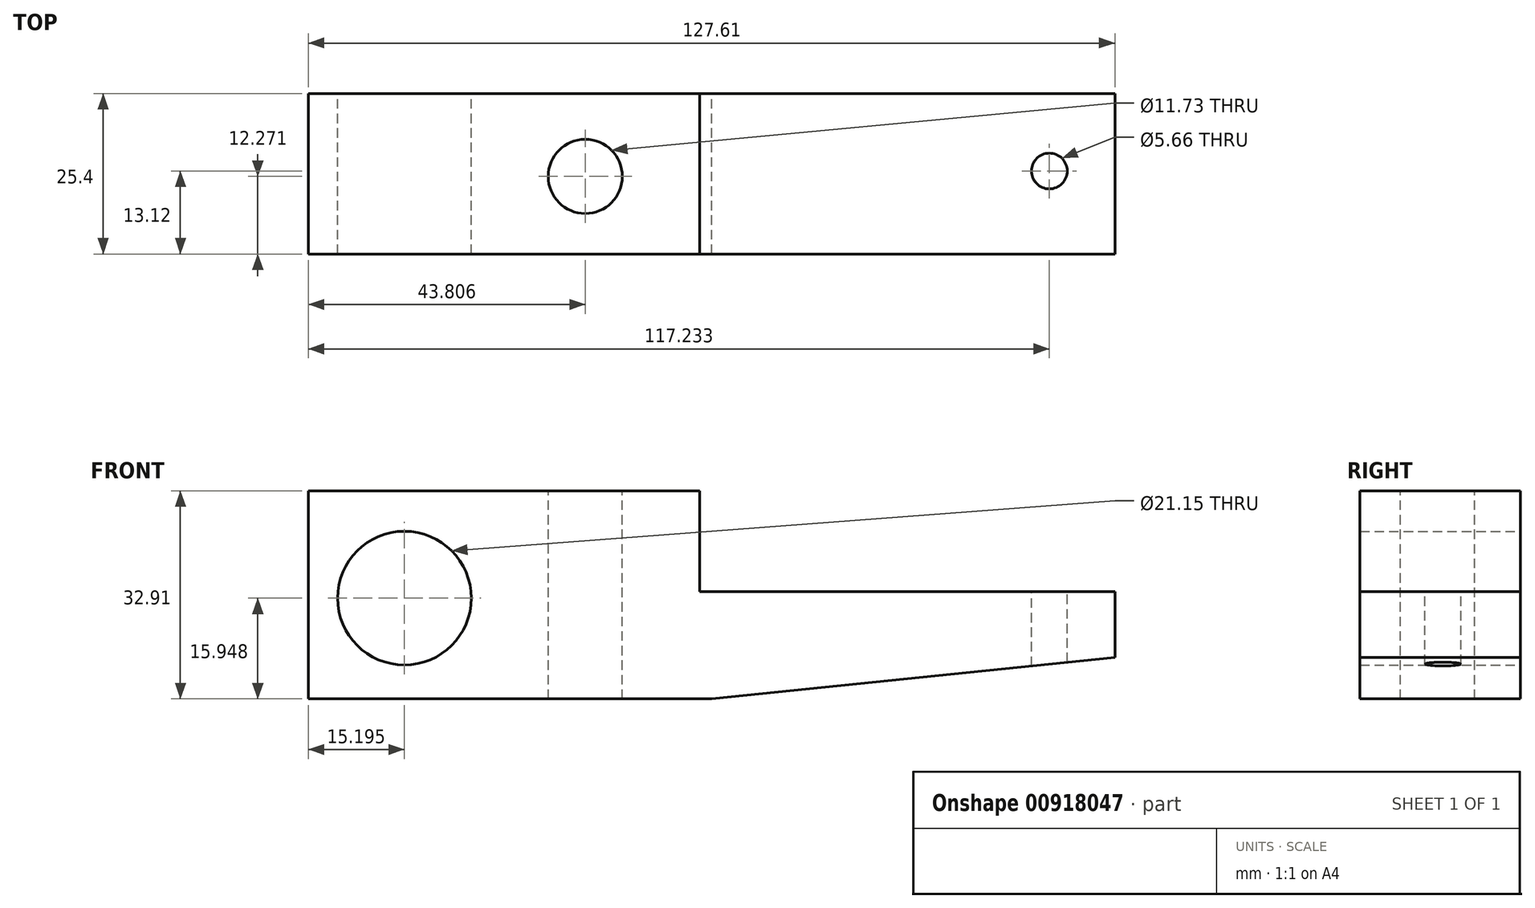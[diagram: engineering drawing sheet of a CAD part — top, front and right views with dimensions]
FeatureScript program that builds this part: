
annotation { "Feature Type Name" : "Feature", "Feature Type Description" : "" }
export const myFeature = defineFeature(function(context is Context, id is Id, definition is map)
    precondition{}
    {
        {
            var Q0;
            Q0=qCreatedBy(makeId("Front.planeOp"),FACE);
            var sketch = newSketch(context, id + "F0", { "sketchPlane" : qUnion([Q0])});
            skLineSegment(sketch, "E0.bottom", {"start": v(-61.9, 38.61) * mm, "end": v(65.7, 38.61) * mm});
            skLineSegment(sketch, "E0.top", {"start": v(-61.9, 5.7) * mm, "end": v(65.7, 5.7) * mm});
            skLineSegment(sketch, "E0.left", {"start": v(-61.9, 38.61) * mm, "end": v(-61.9, 5.7) * mm});
            skLineSegment(sketch, "E0.right", {"start": v(65.7, 38.61) * mm, "end": v(65.7, 5.7) * mm});
            skCircle(sketch, "E1", {"center": v(-46.71, 21.65) * mm, "radius": 10.58 * mm});
            skLineSegment(sketch, "E2", {"start": v(0, 38.61) * mm, "end": v(0, 22.66) * mm});
            skLineSegment(sketch, "E3", {"start": v(0, 22.66) * mm, "end": v(67.98, 22.66) * mm});
            skLineSegment(sketch, "E4", {"start": v(1.9, 5.7) * mm, "end": v(65.7, 12.28) * mm});
            skLineSegment(sketch, "E5", {"start": v(65.7, 12.28) * mm, "end": v(65.7, 22.15) * mm});
            skSolve(sketch);
        }
        {
            var Q0;
            {var subQ4=sQuery(id+"F0.wireOp",EDGE,"E0.left");Q0=makeQuery(id+"F0.imprint","IMPRINT",FACE,{"disambiguationData":[TD([[makeQuery(id+"F0.imprint","IMPRINT",EDGE,{"derivedFrom":subQ4}),1.0]])]});}
            extrude(context, id + "F1", {"entities" : qUnion([Q0]), "depth" : 25.4 * mm, "offsetDistance" : 25.4 * mm});
        }
        {
            var Q0;
            Q0=makeQuery(id+"F1.opExtrude","SWEPT_FACE",FACE,{"disambiguationData":[OSD([sQuery(id+"F0.wireOp",EDGE,"E0.bottom")])]});
            var sketch = newSketch(context, id + "F2", { "sketchPlane" : qUnion([Q0])});
            skCircle(sketch, "E6", {"center": v(-18.1, -13.13) * mm, "radius": 5.87 * mm});
            skSolve(sketch);
        }
        {
            var Q0;
            Q0=makeQuery(id+"F2.imprint","IMPRINT",FACE,{"disambiguationData":[TD([[makeQuery(id+"F2.imprint","IMPRINT",EDGE,{"derivedFrom":sQuery(id+"F2.wireOp",EDGE,"E6")}),1.0]])]});
            var Q1;
            Q1 = qSketchRegion(id + "FZeY1PwOgTfTQHW_0", true);
            extrude(context, id + "F3", {"entities" : qUnion([Q0, Q1]), "operationType" : NewBodyOperationType.REMOVE, "endBound" : BoundingType.THROUGH_ALL, "oppositeDirection" : true, "depth" : 25.4 * mm, "offsetDistance" : 25.4 * mm});
        }
        {
            var Q0;
            Q0=makeQuery(id+"F1.opExtrude","SWEPT_FACE",FACE,{"disambiguationData":[OSD([sQuery(id+"F0.wireOp",EDGE,"E3")])]});
            var sketch = newSketch(context, id + "F4", { "sketchPlane" : qUnion([Q0])});
            skSolve(sketch);
        }
        {
            var Q0;
            {var subQ0=sQuery(id+"F0.wireOp",EDGE,"E3");Q0=makeQuery(id+"F4.imprint","IMPRINT",FACE,{"disambiguationData":[TD([[makeQuery(id+"F4.imprint","IMPRINT",EDGE,{"derivedFrom":makeQuery(id+"F1.opExtrude","CAP_EDGE",EDGE,{"disambiguationData":[OSD([subQ0])],"isStart":true})}),-1.0]])]});}
            var sketch = newSketch(context, id + "F5", { "sketchPlane" : qUnion([Q0])});
            skCircle(sketch, "E7", {"center": v(55.32, -12.28) * mm, "radius": 2.83 * mm});
            skSolve(sketch);
        }
        {
            var Q0;
            Q0 = qSketchRegion(id + "F5", true);
            extrude(context, id + "F6", {"entities" : qUnion([Q0]), "operationType" : NewBodyOperationType.REMOVE, "endBound" : BoundingType.THROUGH_ALL, "oppositeDirection" : true, "depth" : 25.4 * mm, "offsetDistance" : 25.4 * mm});
        }
    });
